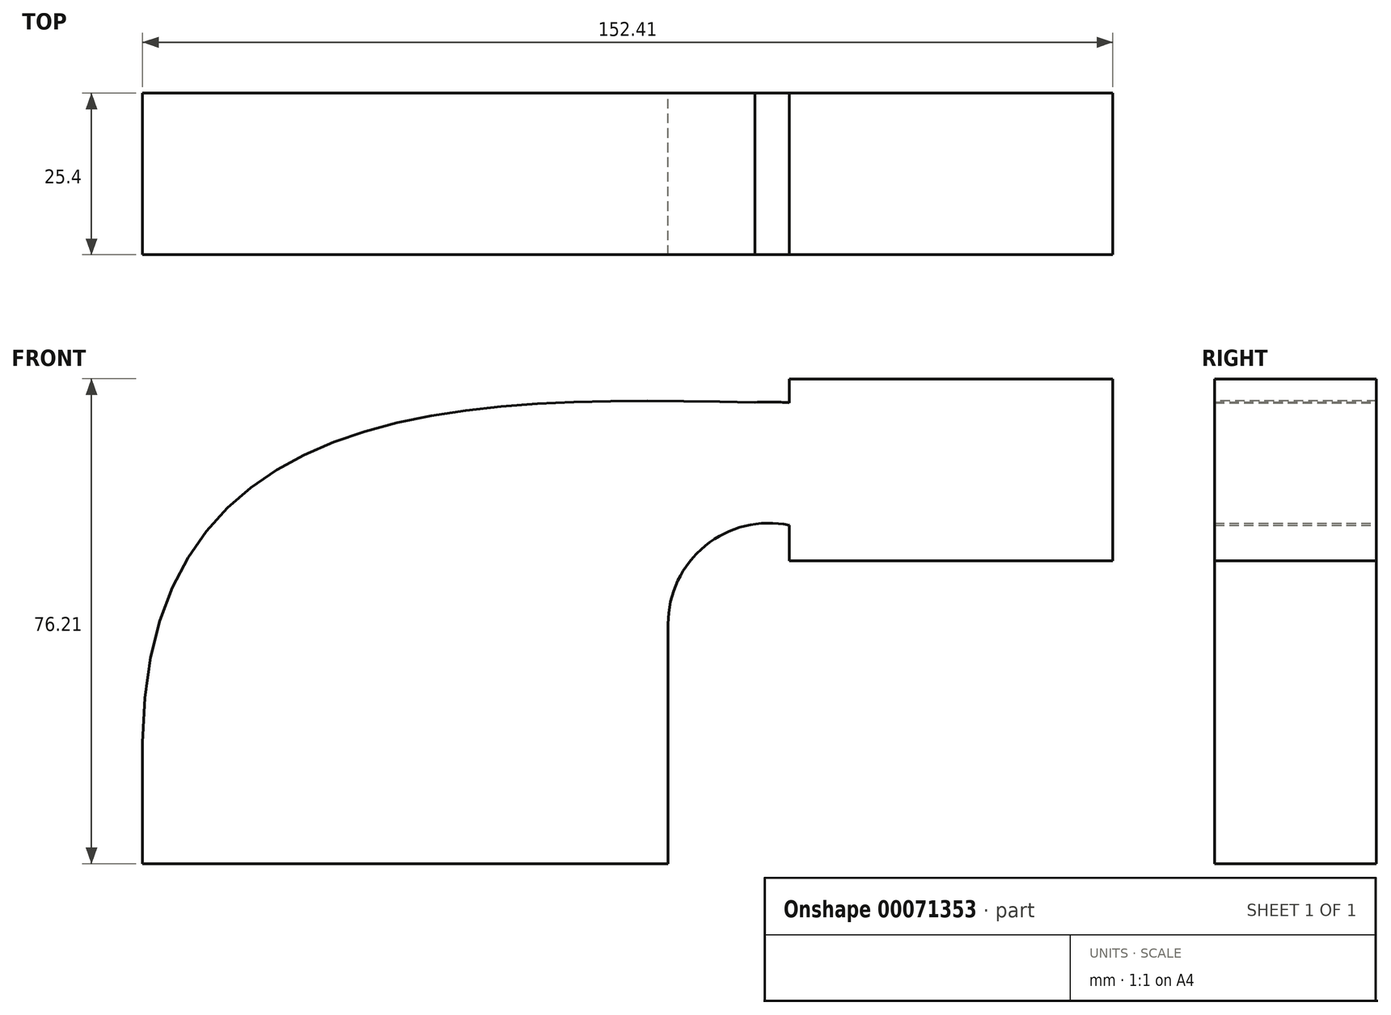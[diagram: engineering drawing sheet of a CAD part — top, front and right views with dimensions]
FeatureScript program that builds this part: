
annotation { "Feature Type Name" : "Feature", "Feature Type Description" : "" }
export const myFeature = defineFeature(function(context is Context, id is Id, definition is map)
    precondition{}
    {
        {
            var Q0;
            Q0=qCreatedBy(makeId("Front.planeOp"),FACE);
            var sketch = newSketch(context, id + "F0", { "sketchPlane" : qUnion([Q0])});
            skLineSegment(sketch, "E0.rect.bottom", {"start": v(-41.28, 9.52) * mm, "end": v(41.27, 9.53) * mm});
            skLineSegment(sketch, "E0.rect.top", {"start": v(-41.28, -9.53) * mm, "end": v(41.28, -9.53) * mm});
            skLineSegment(sketch, "E0.rect.left", {"start": v(-41.28, 9.52) * mm, "end": v(-41.28, -9.53) * mm});
            skLineSegment(sketch, "E0.rect.right", {"start": v(41.27, 9.53) * mm, "end": v(41.28, -9.52) * mm});
            skPoint(sketch, "E0.rect.middle", {"position": v(0, 0) * mm});
            skLineSegment(sketch, "E1.rect.bottom", {"start": v(111.12, 38.1) * mm, "end": v(60.32, 38.1) * mm});
            skLineSegment(sketch, "E1.rect.top", {"start": v(111.12, 66.68) * mm, "end": v(60.32, 66.68) * mm});
            skLineSegment(sketch, "E1.rect.left", {"start": v(111.12, 38.1) * mm, "end": v(111.12, 66.68) * mm});
            skLineSegment(sketch, "E1.rect.right", {"start": v(60.32, 38.1) * mm, "end": v(60.32, 66.68) * mm});
            skPoint(sketch, "E1.rect.middle", {"position": v(85.72, 52.39) * mm});
            skLineSegment(sketch, "E2", {"start": v(41.27, 9.53) * mm, "end": v(41.27, 28.13) * mm});
            skArc(sketch, "E3", {"start": v(41.27, 28.13) * mm, "mid": v(48.24, 41.27) * mm, "end": v(63.03, 42.88) * mm});
            skLineSegment(sketch, "E4", {"start": v(63.03, 42.88) * mm, "end": v(85.69, 42.88) * mm});
            skArc(sketch, "E5.0", {"start": v(22.22, 28.13) * mm, "mid": v(33.6, 53.92) * mm, "end": v(60.32, 62.91) * mm});
            skLineSegment(sketch, "E5.1", {"start": v(22.22, 9.53) * mm, "end": v(22.22, 28.13) * mm});
            skLineSegment(sketch, "E6", {"start": v(60.32, 62.91) * mm, "end": v(91.79, 62.91) * mm});
            skFitSpline(sketch, "E7", {"points": [v(-41.28, 9.53) * mm, v(60.32, 62.91) * mm], "startDerivative": vector(1.12, 176.12) * mm, "endDerivative": vector(128.4, -1.35) * mm});
            skLineSegment(sketch, "E8", {"start": v(85.72, 66.68) * mm, "end": v(85.69, 38.1) * mm});
            skSolve(sketch);
        }
        {
            var Q0;
            Q0 = qSketchRegion(id + "F0", true);
            extrude(context, id + "F1", {"entities" : qUnion([Q0]), "depth" : 25.4 * mm});
        }
    });
